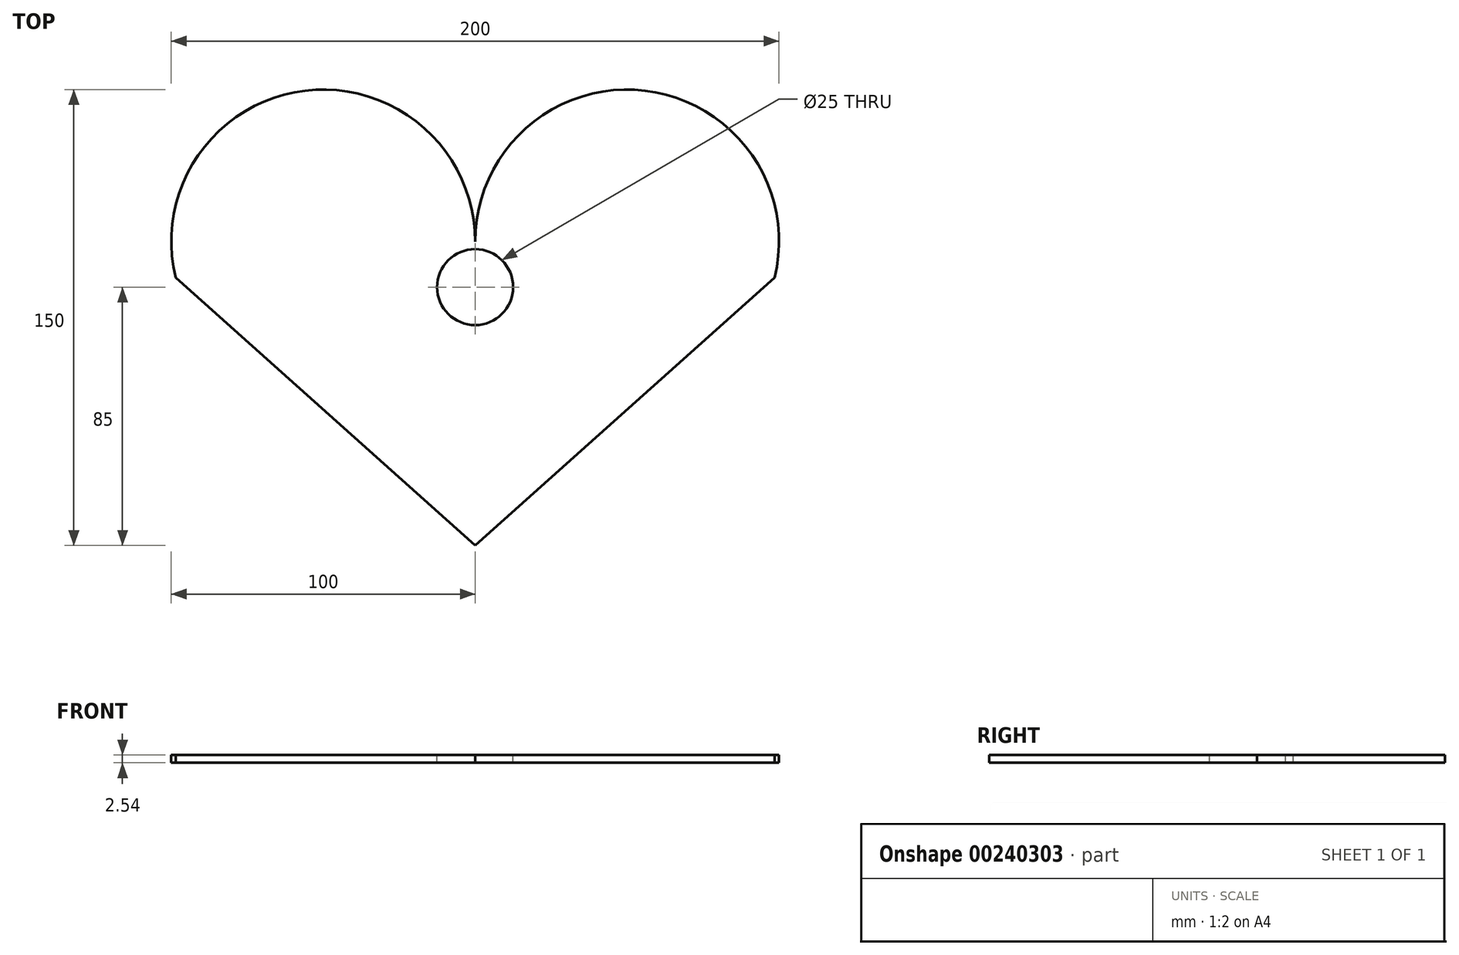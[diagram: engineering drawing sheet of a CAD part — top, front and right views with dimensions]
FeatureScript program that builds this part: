
annotation { "Feature Type Name" : "Feature", "Feature Type Description" : "" }
export const myFeature = defineFeature(function(context is Context, id is Id, definition is map)
    precondition{}
    {
        {
            var Q0;
            Q0=qCreatedBy(makeId("Top.planeOp"),FACE);
            var sketch = newSketch(context, id + "F0", { "sketchPlane" : qUnion([Q0])});
            skLineSegment(sketch, "E0.left", {"start": v(-50, 0) * mm, "end": v(-50, -5.28) * mm, "construction": true});
            skLineSegment(sketch, "E0.right", {"start": v(50, 0) * mm, "end": v(50, -5.28) * mm, "construction": true});
            skPoint(sketch, "E0.middle", {"position": v(0, 0) * mm});
            skArc(sketch, "E1", {"start": v(0, 50) * mm, "mid": v(-55.95, 99.64) * mm, "end": v(-98.58, 38.18) * mm});
            skArc(sketch, "E2", {"start": v(50, 0) * mm, "mid": v(53.18, 0.1) * mm, "end": v(56.35, 0.4) * mm});
            skLineSegment(sketch, "E3", {"start": v(0, -50) * mm, "end": v(-98.58, 38.18) * mm});
            skLineSegment(sketch, "E4", {"start": v(0, -50) * mm, "end": v(98.58, 38.18) * mm});
            skArc(sketch, "E5.trimOffspring", {"start": v(98.58, 38.18) * mm, "mid": v(55.95, 99.64) * mm, "end": v(0, 50) * mm});
            skArc(sketch, "E6.trimOffspring", {"start": v(-56.35, 0.4) * mm, "mid": v(-53.18, 0.1) * mm, "end": v(-50, 0) * mm});
            skPoint(sketch, "E7.orphan", {"position": v(50, -50) * mm});
            skPoint(sketch, "E0.top.start.orphan", {"position": v(-50, -50) * mm});
            skSolve(sketch);
        }
        {
            var Q0;
            {var subQ4=sQuery(id+"F0.wireOp",EDGE,"E1");Q0=makeQuery(id+"F0.imprint","IMPRINT",FACE,{"disambiguationData":[TD([[makeQuery(id+"F0.imprint","IMPRINT",EDGE,{"derivedFrom":subQ4}),1.0]])]});}
            extrude(context, id + "F1", {"entities" : qUnion([Q0]), "depth" : 2.54 * mm});
        }
        {
            var Q0;
            Q0=makeQuery(id+"F1.opExtrude","CAP_FACE",FACE,{"disambiguationData":[OSD([sQuery(id+"F0.wireOp",EDGE,"E1"),sQuery(id+"F0.wireOp",EDGE,"E3"),sQuery(id+"F0.wireOp",EDGE,"E4"),sQuery(id+"F0.wireOp",EDGE,"E5.trimOffspring")])],"isStart":false});
            var sketch = newSketch(context, id + "F2", { "sketchPlane" : qUnion([Q0])});
            skLineSegment(sketch, "E8", {"start": v(0, 0) * mm, "end": v(0, 35) * mm, "construction": true});
            skCircle(sketch, "E9", {"center": v(0, 35) * mm, "radius": 12.5 * mm});
            skSolve(sketch);
        }
        {
            var Q0;
            Q0=makeQuery(id+"F2.imprint","IMPRINT",FACE,{"disambiguationData":[TD([[makeQuery(id+"F2.imprint","IMPRINT",EDGE,{"derivedFrom":sQuery(id+"F2.wireOp",EDGE,"E9")}),1.0]])]});
            extrude(context, id + "F3", {"entities" : qUnion([Q0]), "operationType" : NewBodyOperationType.REMOVE, "oppositeDirection" : true, "depth" : 25.4 * mm});
        }
    });
